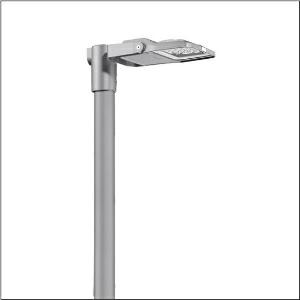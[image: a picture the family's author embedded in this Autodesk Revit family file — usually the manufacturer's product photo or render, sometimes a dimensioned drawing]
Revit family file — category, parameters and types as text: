
# Revit family: floodlight_fl_21_iq_micro___pl64_5xa7762a2e3a_859a
name_source: partatom
category: Lighting Fixtures
units: mm (PartAtom-declared; Revit-internal decimal feet)

## family parameters
Cut with Voids When Loaded = No
Host = Face
Light Source = No
Part Type = Normal
Room Calculation Point = No
Round Connector Dimension = Use Diameter
Shared = No

## types (1)
- --- (1 x LED, 2870 lm, 23.1 W, 3000K)
    Apparent Load = 23 VA
    CIE Flux Codes = 28 80 98 100 100
    Color Rendering = 70
    Color Temperature = 3000K
    Default Elevation = 1800 mm
    Description = Floodlight FL 21 iQ micro, floodlight, primary light control with lens, of PMMA, primary optical cover: protective disc, of toughened safety glass, transparent, light distribution: PL64, light emission: direct distribution, installation type: surface-mounted, LED, High Power LED, rated luminous flux: 2.870lm, luminous efficacy: 124lm/W, light colour: 730, colour temperature: 3000K, control: Auto-Match, Temp-Guard, Night-Set, Smart-Wire, Desk-Remote (wireless, voltage-free reading and setting of iQ features in the workshop via application-optimized NFC function/RFID function), optimised constant luminous flux control (CLO 2.0), Street-Remote, with terminal, 6-pole, mains connection: 220..240V, AC, 50/60Hz, start of lifetime: 23W, end of service life: 24W, reduction: 11W, luminaire housing, of diecast aluminium, powder-coated, Siteco® metallic grey (DB 702S), corrosivity category C5 mid according to DIN EN ISO 12944, sealing non-destructively replaceable, please order mast flange separately, mast bracket, of steel, galvanised, powder-coated, Siteco® metallic grey (DB 702S), protection rating (complete): IP66, insulation class (complete): insulation class II (safety insulation), certification: CE, ENEC, VDE, protection symbol: D, impact resistance: IK07, permissible operating ambient temperature: -40..+40°C, permissible operating ambient temperature for outdoor applications: -40..+50°C, standard: DIN EN 12944, LABS conformity tested according to VDMA 24364:2018-05, packaging unit: 1 piece

Light Distribution: PL64
    Height = 65 mm
    Lamp = 1 x LED
    Lamp Light Flux = 2870 lm
    Lamp Power = 23.1 W
    Lamp count = 1
    Length = 312 mm
    Luminous efficacy = 124 lm/W
    Manufacturer = Siteco
    ModVariant = No
    Model = 5XA7762A2E3A
    Number of Poles = 1
    OnlyDefault = Yes
    Power Factor = 1
    Product Name = Floodlight FL 21 iQ micro | PL64
    Product group = floodlight | pylon annexe
    ProductGroupID = 6200
    Protection Class = Protection class II
    Protection Degree = IP 66
    RLX_Detail_Level = 1
    RLX_Emergency_Light_Flux = 0 lm
    RLX_Emergency_Type = 0
    RLX_Emergency_Type_DB = No
    RlxData = <blob elided: 102037 chars, md5=d2603ca2>
    Socket = socket
    Standby Power = 0 W
    System Light Flux = 2870 lm
    System Power = 23 W
    Type Comments = factory setting: luminous flux: 100 % | dim-lin: 254 | 455 mA
    Type Image = l_1007121.jpg
    URL = http://relux.com
    VarID = @adj_113683
    Voltage = 0 V
    Weight = 0.00 kg
    Width = 230 mm

## geometry (parser evidence)
native form markers: Blend x4, Sweep x12
no freeform markers — native parametric forms only
